# Revit family: cave_wallwash_120-0219
name_source: partatom
category: Lighting Fixtures
units: mm (PartAtom-declared; Revit-internal decimal feet)

## family parameters
Cut with Voids When Loaded = No
Host = Face
Light Source = No
Part Type = Normal
Room Calculation Point = No
Round Connector Dimension = Use Diameter
Shared = No

## types (1)
- 120-0219-K20 (1 x LED, 1182 lm, 13 W, Natural Dim)
    Apparent Load = 13 VA
    Approval mark = CE
    CIE Flux Codes = 87 98 100 100 74
    Color Rendering = 1A/90…99
    Color Temperature = Natural Dim
    Default Elevation = 1800 mm
    Description = CAVE WALLWASH
    Height = 0 mm  [stored 0 ft]
    Lamp = 1 x LED
    Lamp Light Flux = 1182 lm
    Lamp Power = 13 W
    Lamp count = 1
    Length = 140 mm  [stored 0.459318 ft]
    Luminous efficacy = 67 lm/W
    Manufacturer = Prolicht
    ModVariant = No
    Model = 120-0219
    Mounting Place = Ceiling
    Mounting Type = Recessed
    Number of Poles = 1
    OnlyDefault = Yes
    Power Factor = 1
    Product Name = CAVE WALLWASH
    Product group = Trimless recessed spotlights
    ProductGroupID = 412
    Protection Class = Safety extra-low voltage
    Protection Degree = IP 20
    RLX_Detail_Level = 1
    RLX_Emergency_Light_Flux = 0 lm
    RLX_Emergency_Type = 0
    RLX_Emergency_Type_DB = No
    RlxData = <blob elided: 317569 chars, md5=af4044be>
    Socket = socket
    Standby Power = 0 W
    System Light Flux = 877 lm
    System Power = 13 W
    Type Comments = REFLECTOR 20° (20)
    Type Image = 120-0219.jpg
    URL = http://relux.com
    VarID = 120-0219-k20
    Voltage = 0 V
    Weight = 0.00 kg
    Width = 70 mm

note: [stored X ft] marks values corroborated as IEEE doubles in the binary element streams (Revit-internal decimal feet)

## geometry (parser evidence)
native form markers: Sweep x15
no freeform markers — native parametric forms only
